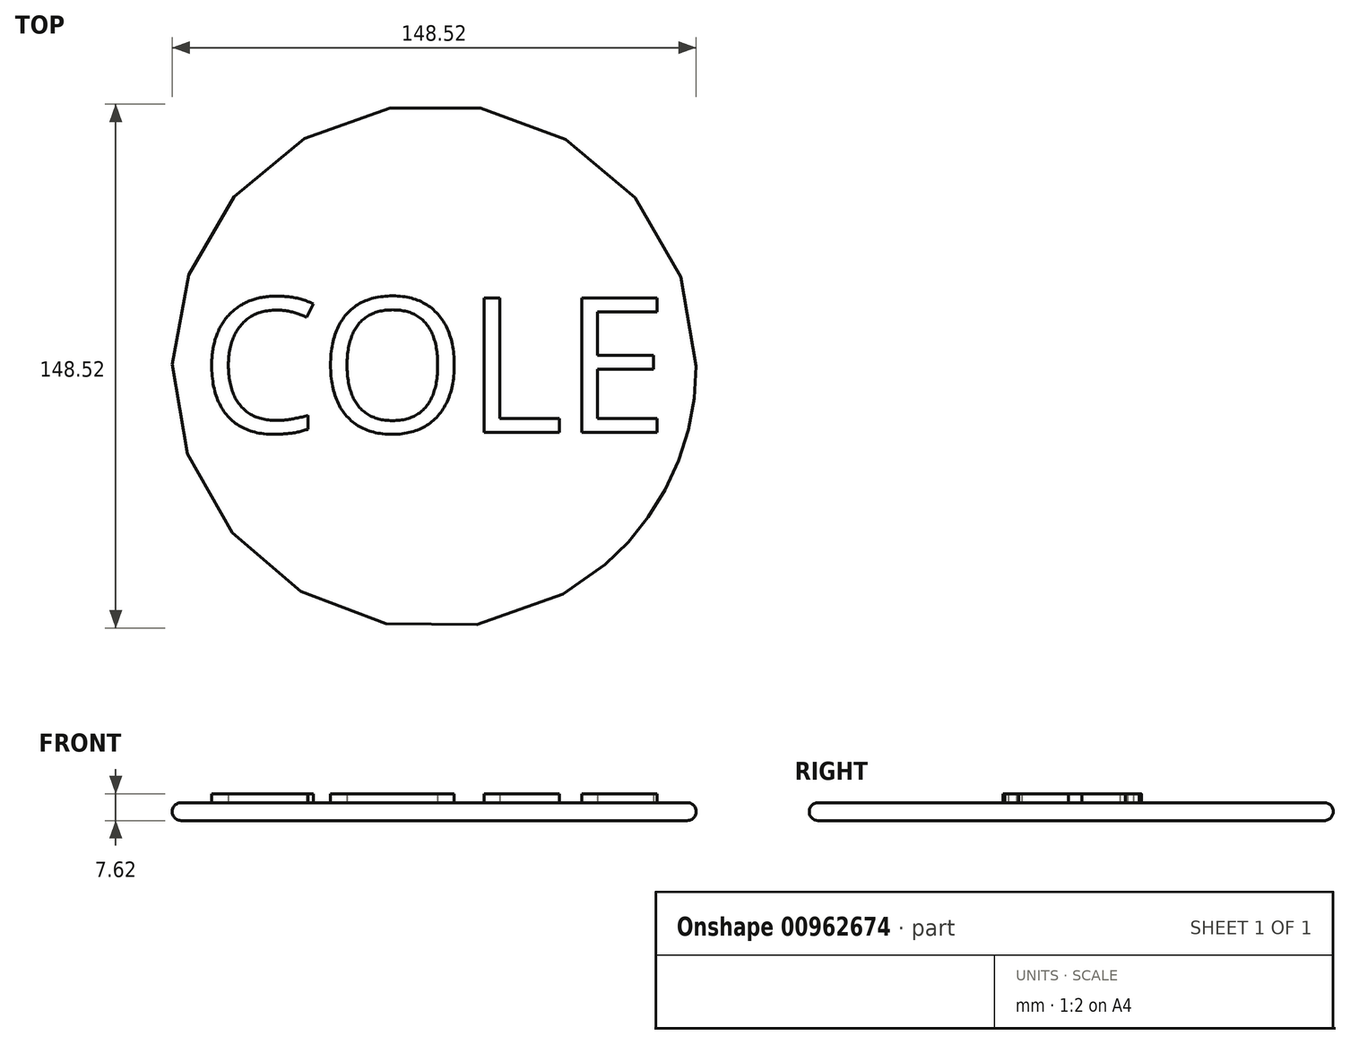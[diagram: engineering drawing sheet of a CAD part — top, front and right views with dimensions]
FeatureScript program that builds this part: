
annotation { "Feature Type Name" : "Feature", "Feature Type Description" : "" }
export const myFeature = defineFeature(function(context is Context, id is Id, definition is map)
    precondition{}
    {
        {
            var Q0;
            Q0=qCreatedBy(makeId("Top.planeOp"),FACE);
            var sketch = newSketch(context, id + "F0", { "sketchPlane" : qUnion([Q0])});
            skCircle(sketch, "E0", {"center": v(0, 0) * mm, "radius": 74.26 * mm});
            skSolve(sketch);
        }
        {
            var Q0;
            Q0=makeQuery(id+"F0.imprint","IMPRINT",FACE,{"disambiguationData":[TD([[makeQuery(id+"F0.imprint","IMPRINT",EDGE,{"derivedFrom":sQuery(id+"F0.wireOp",EDGE,"E0")}),1.0]])]});
            extrude(context, id + "F1", {"entities" : qUnion([Q0]), "depth" : 5.08 * mm, "offsetDistance" : 25.4 * mm});
        }
        {
            var Q0;
            Q0=makeQuery(id+"F1.opExtrude","CAP_FACE",FACE,{"disambiguationData":[OSD([sQuery(id+"F0.wireOp",EDGE,"E0")])],"isStart":false});
            fillet(context, id + "F2", {"entities" : qUnion([Q0]), "radius" : 2.54 * mm, "tangentPropagation" : true, "allowEdgeOverflow" : false});
        }
        {
            var Q0;
            Q0=makeQuery(id+"F1.opExtrude","SWEPT_FACE",FACE,{"disambiguationData":[OSD([sQuery(id+"F0.wireOp",EDGE,"E0")])]});
            fillet(context, id + "F3", {"entities" : qUnion([Q0]), "radius" : 2.54 * mm, "tangentPropagation" : true, "allowEdgeOverflow" : false});
        }
        {
            var Q0;
            Q0=makeQuery(id+"F1.opExtrude","CAP_FACE",FACE,{"disambiguationData":[OSD([sQuery(id+"F0.wireOp",EDGE,"E0")])],"isStart":false});
            var sketch = newSketch(context, id + "F4", { "sketchPlane" : qUnion([Q0])});
            skText(sketch, "E1", { "text": "COLE", "fontName": "OpenSans-Regular.ttf"});
            const initialGuessF4  = {"E1": [-0.06634, -0.01883, 1, 0, 0.03844]};
            skSetInitialGuess(sketch, initialGuessF4);
            skSolve(sketch);
        }
        {
            var Q0;
            Q0 = qSketchRegion(id + "F4", true);
            extrude(context, id + "F5", {"entities" : qUnion([Q0]), "operationType" : NewBodyOperationType.ADD, "depth" : 2.54 * mm, "offsetDistance" : 25.4 * mm});
        }
    });
